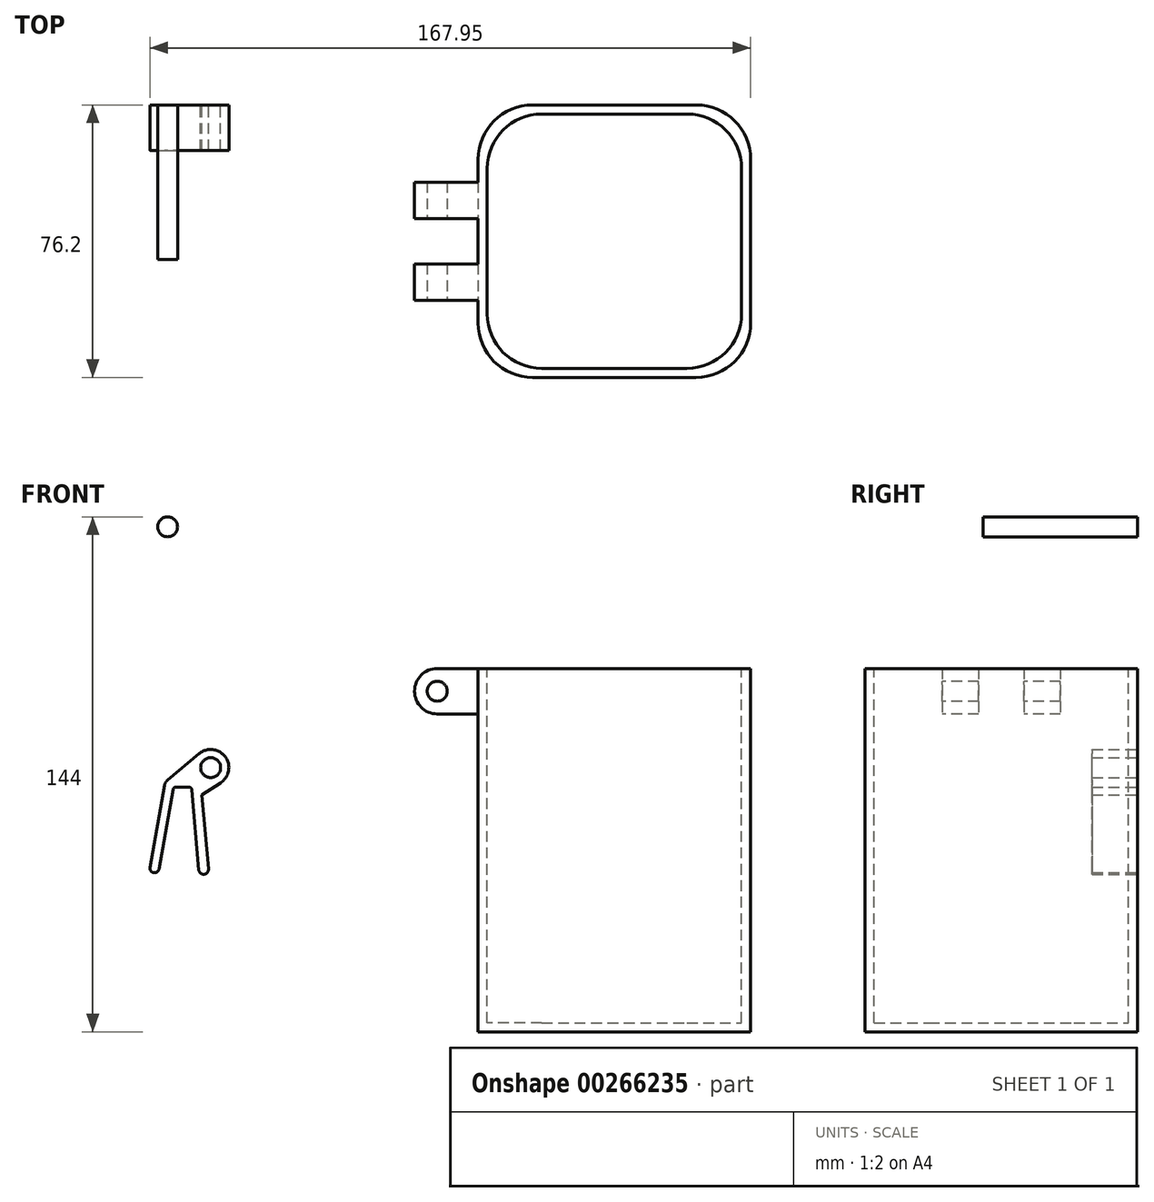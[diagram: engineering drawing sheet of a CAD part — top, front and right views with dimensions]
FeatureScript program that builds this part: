
annotation { "Feature Type Name" : "Feature", "Feature Type Description" : "" }
export const myFeature = defineFeature(function(context is Context, id is Id, definition is map)
    precondition{}
    {
        {
            var Q0;
            Q0=qCreatedBy(makeId("Front.planeOp"),FACE);
            var sketch = newSketch(context, id + "F0", { "sketchPlane" : qUnion([Q0])});
            skLineSegment(sketch, "E0", {"start": v(-57, -42.84) * mm, "end": v(-52.96, -19.93) * mm});
            skLineSegment(sketch, "E1", {"start": v(-42.48, -22.54) * mm, "end": v(-40.66, -43.3) * mm});
            skLineSegment(sketch, "E2.0", {"start": v(-45.32, -21.14) * mm, "end": v(-43.36, -43.55) * mm});
            skLineSegment(sketch, "E2.1", {"start": v(-49.74, -20.37) * mm, "end": v(-46.17, -20.37) * mm});
            skLineSegment(sketch, "E2.2", {"start": v(-54.5, -43.28) * mm, "end": v(-50.58, -21.07) * mm});
            skArc(sketch, "E3", {"start": v(-57, -42.84) * mm, "mid": v(-55.97, -44.31) * mm, "end": v(-54.5, -43.28) * mm});
            skArc(sketch, "E4", {"start": v(-43.36, -43.55) * mm, "mid": v(-41.9, -44.78) * mm, "end": v(-40.66, -43.3) * mm});
            skPoint(sketch, "E5.visualSharp", {"position": v(-52.59, -17.83) * mm});
            skArc(sketch, "E5.filletArc", {"start": v(-52.09, -18.42) * mm, "mid": v(-52.65, -19.1) * mm, "end": v(-52.96, -19.93) * mm});
            skPoint(sketch, "E6.visualSharp", {"position": v(-42.87, -18) * mm});
            skArc(sketch, "E7.filletArc", {"start": v(-49.74, -20.37) * mm, "mid": v(-50.29, -20.57) * mm, "end": v(-50.58, -21.07) * mm});
            skPoint(sketch, "E8.visualSharp", {"position": v(-45.39, -20.37) * mm});
            skArc(sketch, "E8.filletArc", {"start": v(-45.32, -21.14) * mm, "mid": v(-45.6, -20.6) * mm, "end": v(-46.17, -20.37) * mm});
            skArc(sketch, "E9", {"start": v(-37.3, -19.22) * mm, "mid": v(-35.95, -11.93) * mm, "end": v(-43.3, -11.05) * mm});
            skCircle(sketch, "E10", {"center": v(-40.04, -14.94) * mm, "radius": 2.8 * mm});
            skLineSegment(sketch, "E11", {"start": v(-52.09, -18.42) * mm, "end": v(-43.3, -11.05) * mm});
            skLineSegment(sketch, "E12", {"start": v(-42.48, -22.54) * mm, "end": v(-37.3, -19.22) * mm});
            skSolve(sketch);
        }
        {
            var Q0;
            Q0 = qSketchRegion(id + "F0", true);
            extrude(context, id + "F1", {"entities" : qUnion([Q0]), "depth" : 12.7 * mm});
        }
        {
            var Q0;
            Q0=qCreatedBy(makeId("Front.planeOp"),FACE);
            var sketch = newSketch(context, id + "F2", { "sketchPlane" : qUnion([Q0])});
            skLineSegment(sketch, "E13", {"start": v(34.73, -88.8) * mm, "end": v(110.93, -88.8) * mm});
            skLineSegment(sketch, "E14", {"start": v(110.93, -88.8) * mm, "end": v(110.93, 12.8) * mm});
            skLineSegment(sketch, "E15", {"start": v(110.93, 12.8) * mm, "end": v(34.73, 12.8) * mm});
            skLineSegment(sketch, "E16", {"start": v(34.73, 12.8) * mm, "end": v(34.73, 7.2) * mm});
            skLineSegment(sketch, "E17", {"start": v(34.73, -88.8) * mm, "end": v(34.73, 7.2) * mm});
            skSolve(sketch);
        }
        {
            var Q0;
            Q0=makeQuery(id+"F2.imprint","IMPRINT",FACE,{"disambiguationData":[TD([[makeQuery(id+"F2.imprint","IMPRINT",EDGE,{"derivedFrom":sQuery(id+"F2.wireOp",EDGE,"E13")}),1.0]])]});
            extrude(context, id + "F3", {"entities" : qUnion([Q0]), "depth" : 76.2 * mm});
        }
        {
            var Q0;
            Q0=makeQuery(id+"F3.opExtrude","SWEPT_FACE",FACE,{"disambiguationData":[OSD([sQuery(id+"F2.wireOp",EDGE,"E15")])]});
            shell(context, id + "F4", {"entities" : qUnion([Q0]), "thickness" : 2.54 * mm});
        }
        {
            var Q0;
            {var subQ0=sQuery(id+"F2.wireOp",EDGE,"E17");Q0=makeQuery(id+"F4.opShell","OFFSET_EDGE",EDGE,{"disambiguationData":[OSD([subQ0]),TDD([makeQuery(id+"F3.opExtrude","CAP_EDGE",EDGE,{"disambiguationData":[OSD([subQ0])],"isStart":true})])]});}
            var Q1;
            {var subQ0=sQuery(id+"F2.wireOp",EDGE,"E14");Q1=makeQuery(id+"F4.opShell","OFFSET_EDGE",EDGE,{"disambiguationData":[OSD([subQ0]),TDD([makeQuery(id+"F3.opExtrude","CAP_EDGE",EDGE,{"disambiguationData":[OSD([subQ0])],"isStart":true})])]});}
            var Q2;
            {var subQ0=sQuery(id+"F2.wireOp",EDGE,"E17");Q2=makeQuery(id+"F4.opShell","OFFSET_EDGE",EDGE,{"disambiguationData":[OSD([subQ0]),TDD([makeQuery(id+"F3.opExtrude","CAP_EDGE",EDGE,{"disambiguationData":[OSD([subQ0])],"isStart":false})])]});}
            var Q3;
            {var subQ0=sQuery(id+"F2.wireOp",EDGE,"E14");Q3=makeQuery(id+"F4.opShell","OFFSET_EDGE",EDGE,{"disambiguationData":[OSD([subQ0]),TDD([makeQuery(id+"F3.opExtrude","CAP_EDGE",EDGE,{"disambiguationData":[OSD([subQ0])],"isStart":false})])]});}
            fillet(context, id + "F5", {"entities" : qUnion([Q0, Q1, Q2, Q3]), "radius" : 15.24 * mm, "tangentPropagation" : true, "allowEdgeOverflow" : false});
        }
        {
            var Q0;
            Q0=makeQuery(id+"F3.opExtrude","CAP_EDGE",EDGE,{"disambiguationData":[OSD([sQuery(id+"F2.wireOp",EDGE,"E14")])],"isStart":true});
            var Q1;
            Q1=makeQuery(id+"F3.opExtrude","CAP_EDGE",EDGE,{"disambiguationData":[OSD([sQuery(id+"F2.wireOp",EDGE,"E14")])],"isStart":false});
            var Q2;
            Q2=makeQuery(id+"F3.opExtrude","CAP_EDGE",EDGE,{"disambiguationData":[OSD([sQuery(id+"F2.wireOp",EDGE,"E16"),sQuery(id+"F2.wireOp",EDGE,"E17")])],"isStart":true});
            var Q3;
            Q3=makeQuery(id+"F3.opExtrude","CAP_EDGE",EDGE,{"disambiguationData":[OSD([sQuery(id+"F2.wireOp",EDGE,"E16"),sQuery(id+"F2.wireOp",EDGE,"E17")])],"isStart":false});
            fillet(context, id + "F6", {"entities" : qUnion([Q0, Q1, Q2, Q3]), "radius" : 15.24 * mm, "tangentPropagation" : true, "allowEdgeOverflow" : false});
        }
        {
            var Q0;
            Q0=makeQuery(id+"F3.opExtrude","SWEPT_FACE",FACE,{"disambiguationData":[OSD([sQuery(id+"F2.wireOp",EDGE,"E16"),sQuery(id+"F2.wireOp",EDGE,"E17")])]});
            var sketch = newSketch(context, id + "F7", { "sketchPlane" : qUnion([Q0])});
            skLineSegment(sketch, "E18.bottom", {"start": v(21.59, 12.8) * mm, "end": v(31.75, 12.8) * mm});
            skLineSegment(sketch, "E18.top", {"start": v(21.59, 0.1) * mm, "end": v(31.75, 0.1) * mm});
            skLineSegment(sketch, "E18.left", {"start": v(21.59, 12.8) * mm, "end": v(21.59, 0.1) * mm});
            skLineSegment(sketch, "E18.right", {"start": v(31.75, 12.8) * mm, "end": v(31.75, 0.1) * mm});
            skLineSegment(sketch, "E19.bottom", {"start": v(44.45, 12.8) * mm, "end": v(54.6, 12.8) * mm});
            skLineSegment(sketch, "E19.top", {"start": v(44.45, 0.1) * mm, "end": v(54.6, 0.1) * mm});
            skLineSegment(sketch, "E19.left", {"start": v(44.45, 12.8) * mm, "end": v(44.45, 0.1) * mm});
            skLineSegment(sketch, "E19.right", {"start": v(54.6, 12.8) * mm, "end": v(54.6, 0.1) * mm});
            skSolve(sketch);
        }
        {
            var Q0;
            Q0=makeQuery(id+"F7.imprint","IMPRINT",FACE,{"disambiguationData":[TD([[makeQuery(id+"F7.imprint","IMPRINT",EDGE,{"derivedFrom":sQuery(id+"F7.wireOp",EDGE,"E18.bottom")}),1.0]])]});
            var Q1;
            Q1=makeQuery(id+"F7.imprint","IMPRINT",FACE,{"disambiguationData":[TD([[makeQuery(id+"F7.imprint","IMPRINT",EDGE,{"derivedFrom":sQuery(id+"F7.wireOp",EDGE,"E19.bottom")}),1.0]])]});
            extrude(context, id + "F8", {"entities" : qUnion([Q0, Q1]), "operationType" : NewBodyOperationType.ADD, "depth" : 17.78 * mm});
        }
        {
            var Q0;
            Q0=makeQuery(id+"F8.opExtrude","SWEPT_FACE",FACE,{"disambiguationData":[OSD([sQuery(id+"F7.wireOp",EDGE,"E19.right")])]});
            var sketch = newSketch(context, id + "F9", { "sketchPlane" : qUnion([Q0])});
            skCircle(sketch, "E20", {"center": v(23.3, 6.44) * mm, "radius": 6.35 * mm});
            skPoint(sketch, "E20.centerSnap0", {"position": v(16.95, 6.44) * mm});
            skCircle(sketch, "E21", {"center": v(23.3, 6.44) * mm, "radius": 2.8 * mm});
            skSolve(sketch);
        }
        {
            var Q0;
            {var subQ0=sQuery(id+"F9.wireOp",EDGE,"E20");var subQ1=sQuery(id+"F7.wireOp",EDGE,"E19.right");var subQ2=makeQuery(id+"F8.opExtrude","CAP_EDGE",EDGE,{"disambiguationData":[OSD([subQ1])],"isStart":false});var subQ3=makeQuery(id+"F9.imprint","INTERSECT",VERTEX,{"derivedFrom":[subQ2,subQ0]});Q0=makeQuery(id+"F9.imprint","IMPRINT",FACE,{"disambiguationData":[TD([[makeQuery(id+"F9.imprint","IMPRINT",EDGE,{"disambiguationData":[TD([[subQ3,-1.0]])],"derivedFrom":subQ0}),-1.0]])]});}
            var Q1;
            {var subQ0=sQuery(id+"F9.wireOp",EDGE,"E20");var subQ1=sQuery(id+"F7.wireOp",EDGE,"E19.right");var subQ2=makeQuery(id+"F8.opExtrude","CAP_EDGE",EDGE,{"disambiguationData":[OSD([subQ1])],"isStart":false});var subQ3=makeQuery(id+"F9.imprint","INTERSECT",VERTEX,{"derivedFrom":[subQ2,subQ0]});Q1=makeQuery(id+"F9.imprint","IMPRINT",FACE,{"disambiguationData":[TD([[makeQuery(id+"F9.imprint","IMPRINT",EDGE,{"disambiguationData":[TD([[subQ3,1.0]])],"derivedFrom":subQ0}),-1.0]])]});}
            extrude(context, id + "F10", {"entities" : qUnion([Q0, Q1]), "operationType" : NewBodyOperationType.REMOVE, "oppositeDirection" : true, "depth" : 33.02 * mm});
        }
        {
            var Q0;
            Q0=makeQuery(id+"F9.imprint","IMPRINT",FACE,{"disambiguationData":[TD([[makeQuery(id+"F9.imprint","IMPRINT",EDGE,{"derivedFrom":sQuery(id+"F9.wireOp",EDGE,"E21")}),1.0]])]});
            extrude(context, id + "F11", {"entities" : qUnion([Q0]), "operationType" : NewBodyOperationType.REMOVE, "oppositeDirection" : true, "depth" : 33.02 * mm});
        }
        {
            var Q0;
            Q0=qCreatedBy(makeId("Front.planeOp"),FACE);
            var sketch = newSketch(context, id + "F12", { "sketchPlane" : qUnion([Q0])});
            skCircle(sketch, "E22", {"center": v(-52.08, 52.4) * mm, "radius": 2.78 * mm});
            skSolve(sketch);
        }
        {
            var Q0;
            Q0=makeQuery(id+"F12.imprint","IMPRINT",FACE,{"disambiguationData":[TD([[makeQuery(id+"F12.imprint","IMPRINT",EDGE,{"derivedFrom":sQuery(id+"F12.wireOp",EDGE,"E22")}),1.0]])]});
            extrude(context, id + "F13", {"entities" : qUnion([Q0]), "depth" : 43.18 * mm});
        }
    });
